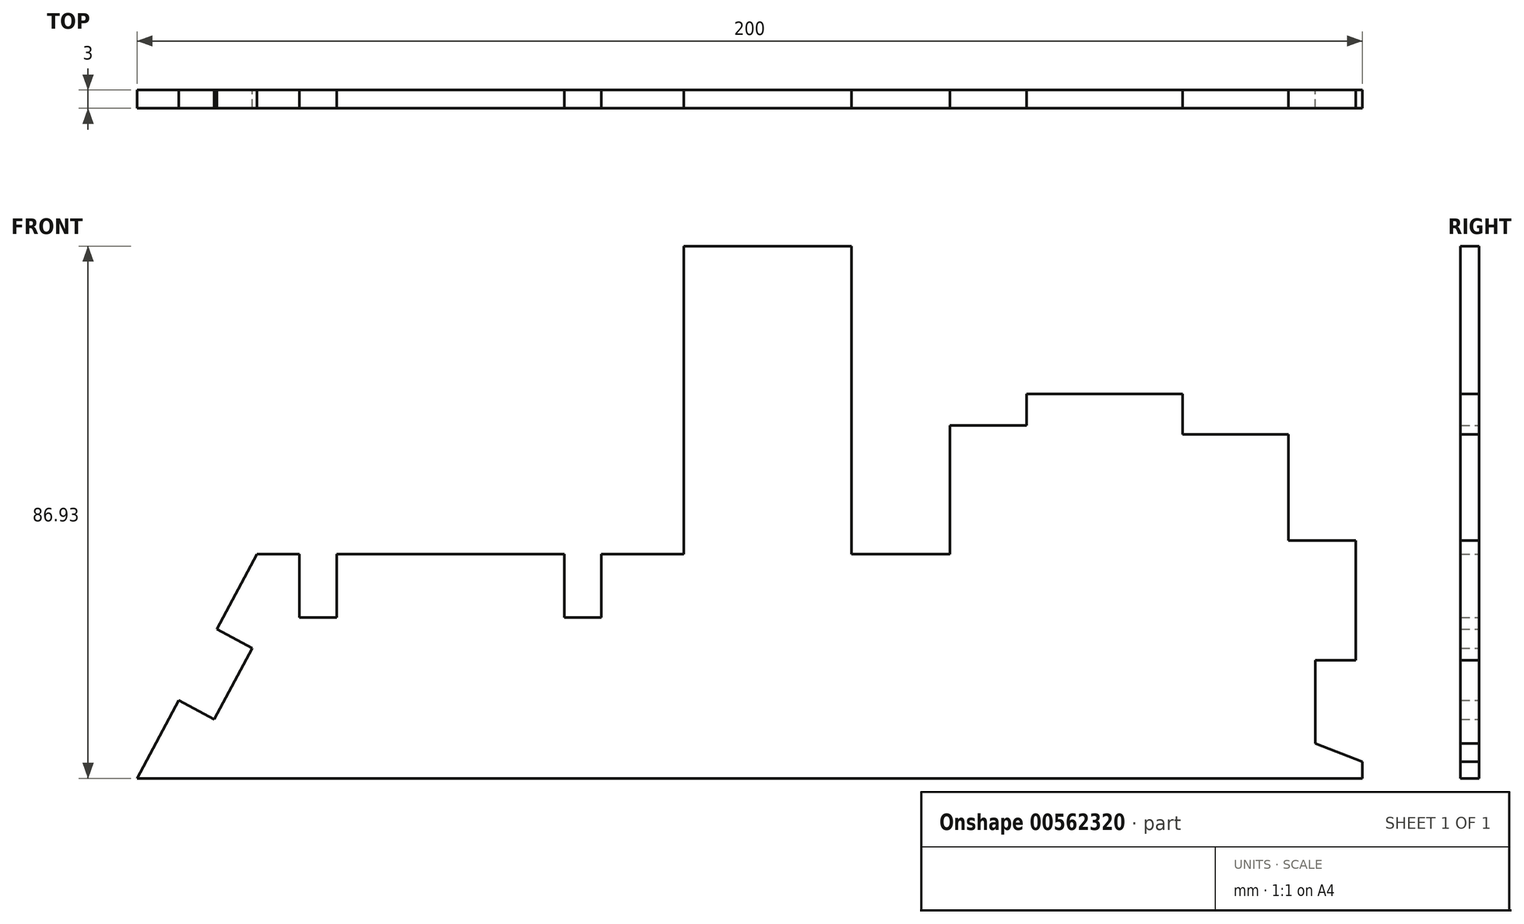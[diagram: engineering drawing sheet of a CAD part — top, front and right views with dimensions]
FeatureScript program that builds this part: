
annotation { "Feature Type Name" : "Feature", "Feature Type Description" : "" }
export const myFeature = defineFeature(function(context is Context, id is Id, definition is map)
    precondition{}
    {
        {
            var Q0;
            Q0=qCreatedBy(makeId("Front.planeOp"),FACE);
            var sketch = newSketch(context, id + "F0", { "sketchPlane" : qUnion([Q0])});
            skLineSegment(sketch, "E0", {"start": v(-93.67, -31.08) * mm, "end": v(106.33, -31.08) * mm});
            skLineSegment(sketch, "E1", {"start": v(106.33, -31.08) * mm, "end": v(106.33, -28.35) * mm});
            skLineSegment(sketch, "E2", {"start": v(106.33, -28.35) * mm, "end": v(98.59, -25.4) * mm});
            skLineSegment(sketch, "E3", {"start": v(98.59, -25.4) * mm, "end": v(98.59, -11.77) * mm});
            skLineSegment(sketch, "E4", {"start": v(98.59, -11.77) * mm, "end": v(105.22, -11.77) * mm});
            skLineSegment(sketch, "E5", {"start": v(105.22, -11.77) * mm, "end": v(105.22, 7.76) * mm});
            skLineSegment(sketch, "E6", {"start": v(105.22, 7.76) * mm, "end": v(94.26, 7.76) * mm});
            skLineSegment(sketch, "E7", {"start": v(94.26, 7.76) * mm, "end": v(94.26, 25.09) * mm});
            skLineSegment(sketch, "E8", {"start": v(94.26, 25.09) * mm, "end": v(76.94, 25.09) * mm});
            skLineSegment(sketch, "E9", {"start": v(76.94, 25.09) * mm, "end": v(76.94, 31.72) * mm});
            skLineSegment(sketch, "E10", {"start": v(76.94, 31.72) * mm, "end": v(51.5, 31.72) * mm});
            skLineSegment(sketch, "E11", {"start": v(51.5, 31.72) * mm, "end": v(51.5, 26.56) * mm});
            skLineSegment(sketch, "E12", {"start": v(51.5, 26.56) * mm, "end": v(38.97, 26.56) * mm});
            skLineSegment(sketch, "E13", {"start": v(38.97, 26.56) * mm, "end": v(38.97, 5.55) * mm});
            skLineSegment(sketch, "E14", {"start": v(38.97, 5.55) * mm, "end": v(36.76, 5.55) * mm});
            skLineSegment(sketch, "E15", {"start": v(36.76, 5.55) * mm, "end": v(22.95, 5.55) * mm});
            skLineSegment(sketch, "E16", {"start": v(22.95, 5.55) * mm, "end": v(22.95, 55.85) * mm});
            skLineSegment(sketch, "E17", {"start": v(22.95, 55.85) * mm, "end": v(-4.42, 55.85) * mm});
            skLineSegment(sketch, "E18", {"start": v(-4.42, 55.85) * mm, "end": v(-4.42, 5.55) * mm});
            skLineSegment(sketch, "E19", {"start": v(-4.42, 5.55) * mm, "end": v(-17.88, 5.55) * mm});
            skLineSegment(sketch, "E20", {"start": v(-17.88, 5.55) * mm, "end": v(-17.88, -4.84) * mm});
            skLineSegment(sketch, "E21", {"start": v(-17.88, -4.84) * mm, "end": v(-23.96, -4.84) * mm});
            skLineSegment(sketch, "E22", {"start": v(-23.96, -4.84) * mm, "end": v(-23.96, 5.55) * mm});
            skLineSegment(sketch, "E23", {"start": v(-23.96, 5.55) * mm, "end": v(-61.08, 5.55) * mm});
            skLineSegment(sketch, "E24", {"start": v(-61.08, 5.55) * mm, "end": v(-61.08, -4.84) * mm});
            skLineSegment(sketch, "E25", {"start": v(-61.08, -4.84) * mm, "end": v(-67.16, -4.84) * mm});
            skLineSegment(sketch, "E26", {"start": v(-67.16, -4.84) * mm, "end": v(-67.16, 5.55) * mm});
            skLineSegment(sketch, "E27", {"start": v(-67.16, 5.55) * mm, "end": v(-74.08, 5.55) * mm});
            skLineSegment(sketch, "E28", {"start": v(-74.08, 5.55) * mm, "end": v(-80.66, -6.75) * mm});
            skLineSegment(sketch, "E29", {"start": v(-80.66, -6.75) * mm, "end": v(-74.9, -9.84) * mm});
            skLineSegment(sketch, "E30", {"start": v(-74.9, -9.84) * mm, "end": v(-81.1, -21.44) * mm});
            skLineSegment(sketch, "E31", {"start": v(-81.1, -21.44) * mm, "end": v(-86.87, -18.36) * mm});
            skLineSegment(sketch, "E32", {"start": v(-86.87, -18.36) * mm, "end": v(-93.67, -31.08) * mm});
            skSolve(sketch);
        }
        {
            var Q0;
            Q0=makeQuery(id+"F0.imprint","IMPRINT",FACE,{"disambiguationData":[TD([[makeQuery(id+"F0.imprint","IMPRINT",EDGE,{"derivedFrom":sQuery(id+"F0.wireOp",EDGE,"E0")}),1.0]])]});
            extrude(context, id + "F1", {"entities" : qUnion([Q0]), "endBound" : BoundingType.SYMMETRIC, "depth" : 3 * mm, "offsetDistance" : 25.4 * mm});
        }
    });
